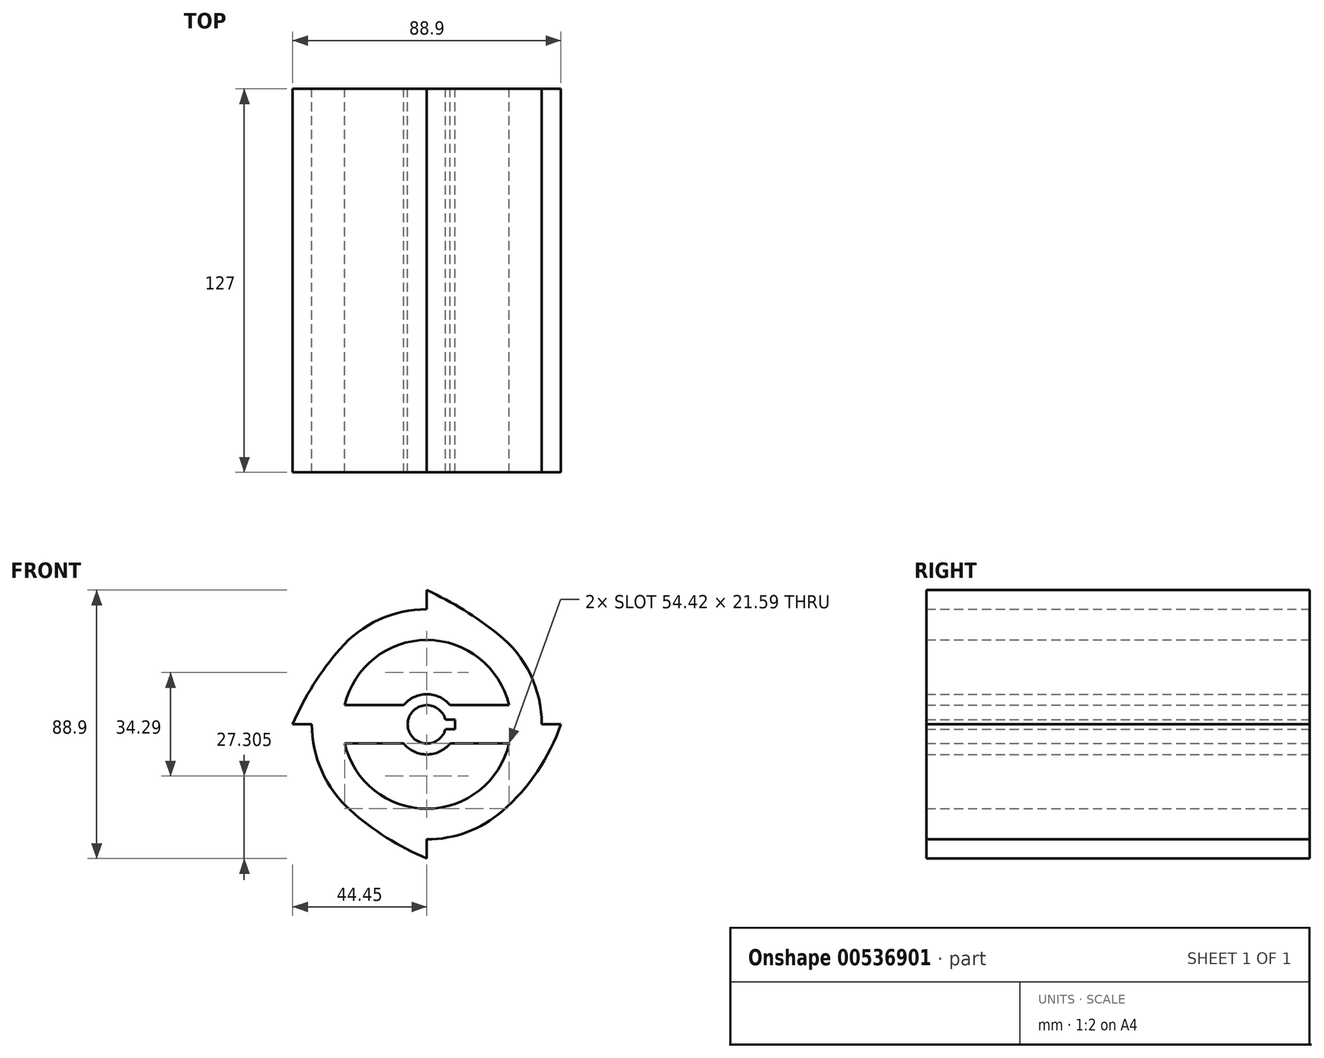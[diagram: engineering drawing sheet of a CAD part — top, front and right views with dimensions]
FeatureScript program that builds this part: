
annotation { "Feature Type Name" : "Feature", "Feature Type Description" : "" }
export const myFeature = defineFeature(function(context is Context, id is Id, definition is map)
    precondition{}
    {
        {
            var Q0;
            Q0=qCreatedBy(makeId("Front.planeOp"),FACE);
            var sketch = newSketch(context, id + "F0", { "sketchPlane" : qUnion([Q0])});
            skCircle(sketch, "E0", {"center": v(0, 0) * mm, "radius": 38.1 * mm});
            skLineSegment(sketch, "E1", {"start": v(-44.45, 0) * mm, "end": v(44.45, 0) * mm});
            skArc(sketch, "E2", {"start": v(23.7, 29.83) * mm, "mid": v(12.29, 37.84) * mm, "end": v(0, 44.45) * mm});
            skArc(sketch, "E3", {"start": v(-28.78, 24.96) * mm, "mid": v(-37.58, 13.09) * mm, "end": v(-44.45, 0) * mm});
            skArc(sketch, "E4", {"start": v(-25.36, -28.44) * mm, "mid": v(-13.34, -37.5) * mm, "end": v(0, -44.45) * mm});
            skArc(sketch, "E5", {"start": v(25.05, -28.7) * mm, "mid": v(36.62, -15.62) * mm, "end": v(44.45, 0) * mm});
            skArc(sketch, "E6", {"start": v(27.2, 6.35) * mm, "mid": v(0, 27.94) * mm, "end": v(-27.2, 6.35) * mm});
            skArc(sketch, "E7", {"start": v(-27.2, -6.35) * mm, "mid": v(0, -27.94) * mm, "end": v(27.2, -6.35) * mm});
            skCircle(sketch, "E8", {"center": v(0, 0) * mm, "radius": 6.35 * mm});
            skLineSegment(sketch, "E9.bottom", {"start": v(-9.4, 1.59) * mm, "end": v(9.4, 1.59) * mm});
            skLineSegment(sketch, "E9.top", {"start": v(-9.4, -1.59) * mm, "end": v(9.4, -1.59) * mm});
            skLineSegment(sketch, "E9.left", {"start": v(-9.4, 1.59) * mm, "end": v(-9.4, -1.59) * mm});
            skLineSegment(sketch, "E9.right", {"start": v(9.4, 1.59) * mm, "end": v(9.4, -1.59) * mm});
            skLineSegment(sketch, "E10", {"start": v(-27.2, -6.35) * mm, "end": v(-7.7, -6.35) * mm});
            skLineSegment(sketch, "E11", {"start": v(-27.2, 6.35) * mm, "end": v(-7.7, 6.35) * mm});
            skLineSegment(sketch, "E12", {"start": v(27.2, -6.35) * mm, "end": v(7.7, -6.35) * mm});
            skLineSegment(sketch, "E13", {"start": v(27.2, 6.35) * mm, "end": v(7.7, 6.35) * mm});
            skCircle(sketch, "E14", {"center": v(0, 0) * mm, "radius": 9.97 * mm});
            skLineSegment(sketch, "E15", {"start": v(0, -44.45) * mm, "end": v(0, -38.1) * mm});
            skLineSegment(sketch, "E16", {"start": v(0, 44.45) * mm, "end": v(0, 38.1) * mm});
            skSolve(sketch);
        }
        {
            var Q0;
            Q0=qSketchRegion(id+"F0",true);
            var Q1;
            {var subQ5=sQuery(id+"F0.wireOp",EDGE,"E14");var subQ6=sQuery(id+"F0.wireOp",EDGE,"E1");var subQ7=makeQuery(id+"F0.imprint","INTERSECT",VERTEX,{"disambiguationData":[OD(0.0)],"derivedFrom":[subQ6,subQ5]});Q1=makeQuery(id+"F0.imprint","IMPRINT",FACE,{"disambiguationData":[TD([[makeQuery(id+"F0.imprint","IMPRINT",EDGE,{"disambiguationData":[TD([[subQ7,-1.0]])],"derivedFrom":subQ6}),-1.0]])]});}
            var Q2;
            {var subQ6=sQuery(id+"F0.wireOp",EDGE,"E1");var subQ10=sQuery(id+"F0.wireOp",EDGE,"E14");var subQ12=makeQuery(id+"F0.imprint","INTERSECT",VERTEX,{"disambiguationData":[OD(0.0)],"derivedFrom":[subQ6,subQ10]});Q2=makeQuery(id+"F0.imprint","IMPRINT",FACE,{"disambiguationData":[TD([[makeQuery(id+"F0.imprint","IMPRINT",EDGE,{"disambiguationData":[TD([[subQ12,-1.0]])],"derivedFrom":subQ6}),1.0]])]});}
            var Q3;
            {var subQ0=sQuery(id+"F0.wireOp",EDGE,"E9.left");var subQ1=sQuery(id+"F0.wireOp",EDGE,"E1");var subQ2=makeQuery(id+"F0.imprint","INTERSECT",VERTEX,{"derivedFrom":[subQ1,subQ0]});Q3=makeQuery(id+"F0.imprint","IMPRINT",FACE,{"disambiguationData":[TD([[makeQuery(id+"F0.imprint","IMPRINT",EDGE,{"disambiguationData":[TD([[subQ2,-1.0]])],"derivedFrom":subQ1}),1.0]])]});}
            var Q4;
            {var subQ0=sQuery(id+"F0.wireOp",EDGE,"E9.left");var subQ1=sQuery(id+"F0.wireOp",EDGE,"E1");var subQ2=makeQuery(id+"F0.imprint","INTERSECT",VERTEX,{"derivedFrom":[subQ1,subQ0]});Q4=makeQuery(id+"F0.imprint","IMPRINT",FACE,{"disambiguationData":[TD([[makeQuery(id+"F0.imprint","IMPRINT",EDGE,{"disambiguationData":[TD([[subQ2,-1.0]])],"derivedFrom":subQ1}),-1.0]])]});}
            extrude(context, id + "F1", {"entities" : qUnion([Q0, Q1, Q2, Q3, Q4]), "depth" : 127 * mm, "offsetDistance" : 25.4 * mm});
        }
    });
